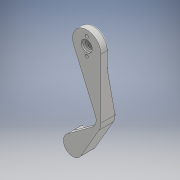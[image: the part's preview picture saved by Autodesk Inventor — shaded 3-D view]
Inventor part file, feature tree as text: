
AUTODESK INVENTOR PART (.ipt)
format: ipt  version: 2017 (Build 210142000, 142)  size: 346,624 bytes
history: native  units: mm
features: sketch x6, extrude x5, fillet x3, hole x2
ambient origin geometry x8: Origin, YZ Plane, XZ Plane, XY Plane, X Axis, Y Axis, Z Axis, Center Point
bodies: Solid1 (feature_tree)
feature tree (16):
  extrude  "Extrusion1"  Depth=9.0mm
  extrude  "Extrusion2"  Depth=6.0mm
  extrude  "Extrusion4"  Depth=23.0mm
  hole  "Hole1"  [1 undecoded]
  fillet  "Fillet1"  Radius=3.0mm
  fillet  "Fillet2"  Radius=9.0mm
  fillet  "Fillet4"  Radius=17.0mm
  extrude  "Extrusion5"  Depth=7.0mm TaperAngle=0.0deg
  hole  "Hole3"  [1 undecoded]
  extrude  "Extrusion6"  Depth=1.0mm
  sketch  "Sketch1"  dims[d0=38.0mm d2=9.0mm]
  sketch  "Sketch3"  dims[d4=9.0mm d7=6.0mm]
  sketch  "Sketch5"  dims[d8=30.0deg d9=23.0mm]
  sketch  "Sketch6"  dims[d10=6.0mm d11=3.0mm d12=3.0mm d13=0.0mm d22=9.0mm d23=17.0mm]
  sketch  "Sketch8"  dims[d25=5.0mm d29=7.0mm d30=0.0mm]
  sketch  "Sketch9"  dims[d34=5.0mm d35=60.0mm d36=28.0mm d37=20.0mm d38=0.0mm d39=18.0mm d40=11.0mm d41=5.5mm d42=5.5mm d43=2.0mm d44=6.0mm d45=4.0mm d46=2.5mm d47=90.0deg d48=8.0mm d49=20.594885mm d52=3.0mm d62=2.0mm d63=2.0mm d65=1.0mm d66=5.0mm d67=10.0mm d68=0.0mm d82=10.0mm d83=10.0mm d71=7.0mm d72=6.0mm d73=4.0mm d74=2.0mm d75=90.0deg d76=1.0mm d77=20.594885mm d80=2.5mm d81=0.0mm d78=1.0mm d79=1.0mm]
note: 2 required parameter values undecoded (feature->parameter linkage not recoverable at this tier; creation-order binding heuristic only, values carry confidence <= 0.55)
